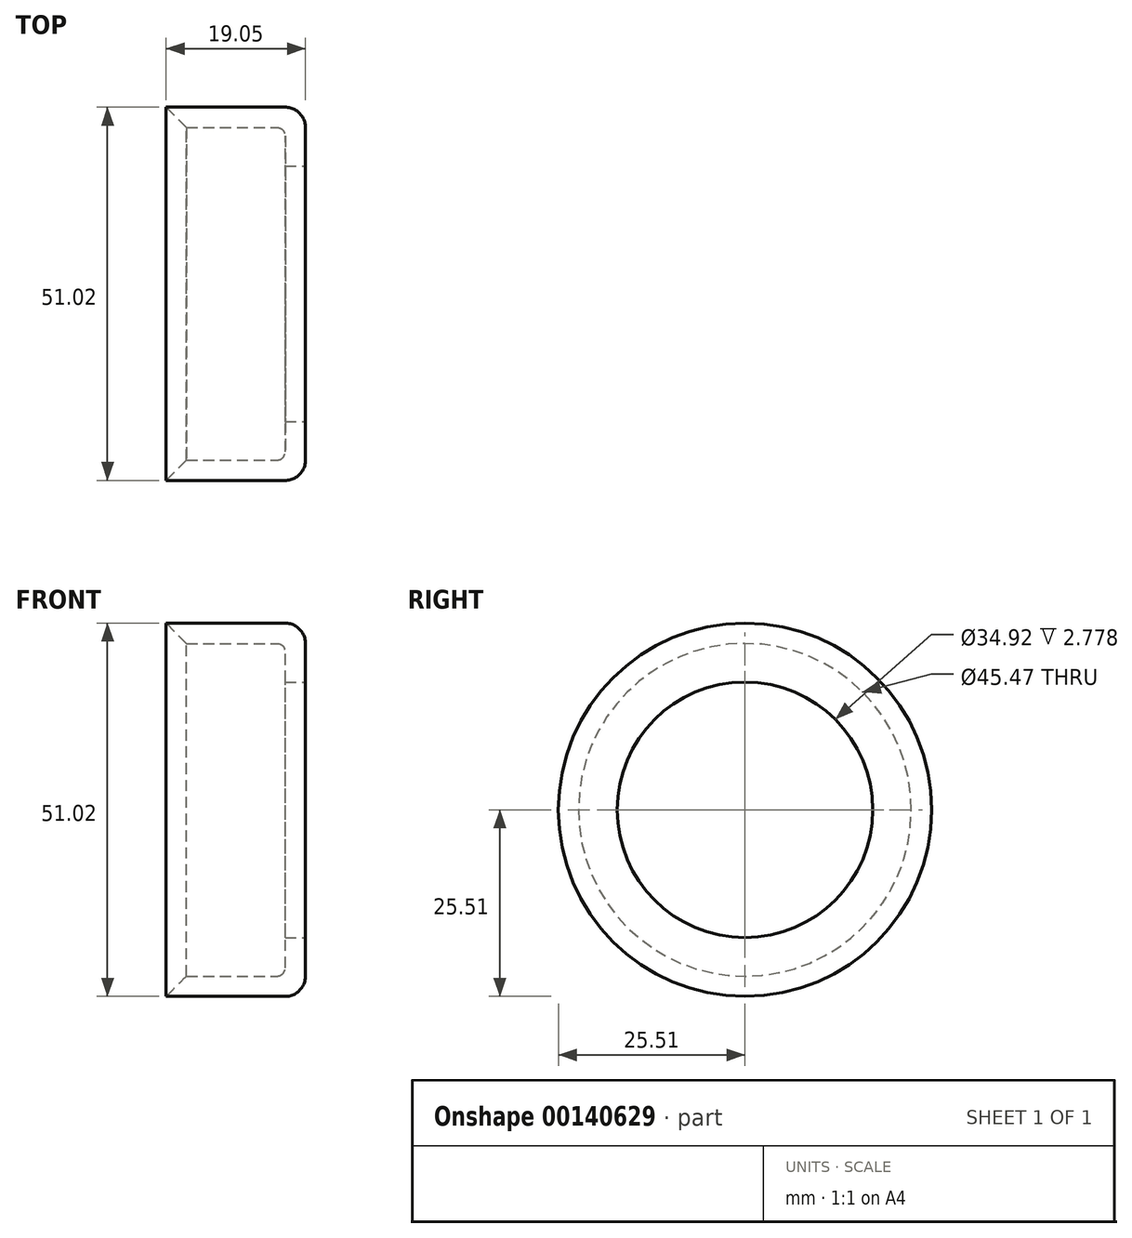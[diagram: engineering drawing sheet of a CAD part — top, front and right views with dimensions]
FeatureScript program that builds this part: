
annotation { "Feature Type Name" : "Feature", "Feature Type Description" : "" }
export const myFeature = defineFeature(function(context is Context, id is Id, definition is map)
    precondition{}
    {
        {
            var Q0;
            Q0=qCreatedBy(makeId("Top.planeOp"),FACE);
            var sketch = newSketch(context, id + "F0", { "sketchPlane" : qUnion([Q0])});
            skLineSegment(sketch, "E0", {"start": v(0, 0) * mm, "end": v(-19.05, 0) * mm});
            skLineSegment(sketch, "E1.0", {"start": v(-2.8, 25.51) * mm, "end": v(-19.05, 25.51) * mm});
            skLineSegment(sketch, "E2.0", {"start": v(-3.92, 22.74) * mm, "end": v(-16.27, 22.74) * mm});
            skLineSegment(sketch, "E3.0", {"start": v(0, 17.46) * mm, "end": v(-2.78, 17.46) * mm});
            skLineSegment(sketch, "E4", {"start": v(0, 22.72) * mm, "end": v(0, 17.46) * mm});
            skLineSegment(sketch, "E5.0", {"start": v(-2.78, 21.6) * mm, "end": v(-2.78, 17.46) * mm});
            skLineSegment(sketch, "E6", {"start": v(-19.05, 25.51) * mm, "end": v(-16.27, 22.74) * mm});
            skPoint(sketch, "E7.visualSharp", {"position": v(-2.78, 22.74) * mm});
            skArc(sketch, "E7.filletArc", {"start": v(-2.78, 21.6) * mm, "mid": v(-3.11, 22.4) * mm, "end": v(-3.92, 22.74) * mm});
            skPoint(sketch, "E8.visualSharp", {"position": v(0, 25.51) * mm});
            skArc(sketch, "E8.filletArc", {"start": v(0, 22.72) * mm, "mid": v(-0.82, 24.7) * mm, "end": v(-2.8, 25.51) * mm});
            skSolve(sketch);
        }
        {
            var Q0;
            Q0=makeQuery(id+"F0.imprint","IMPRINT",FACE,{"disambiguationData":[TD([[makeQuery(id+"F0.imprint","IMPRINT",EDGE,{"derivedFrom":sQuery(id+"F0.wireOp",EDGE,"E1.0")}),1.0]])]});
            var Q1;
            Q1=sQuery(id+"F0.wireOp",EDGE,"E0");
            revolve(context, id + "F1", {"entities" : qUnion([Q0]), "axis" : qUnion([Q1]), "revolveType" : RevolveType.FULL});
        }
    });
